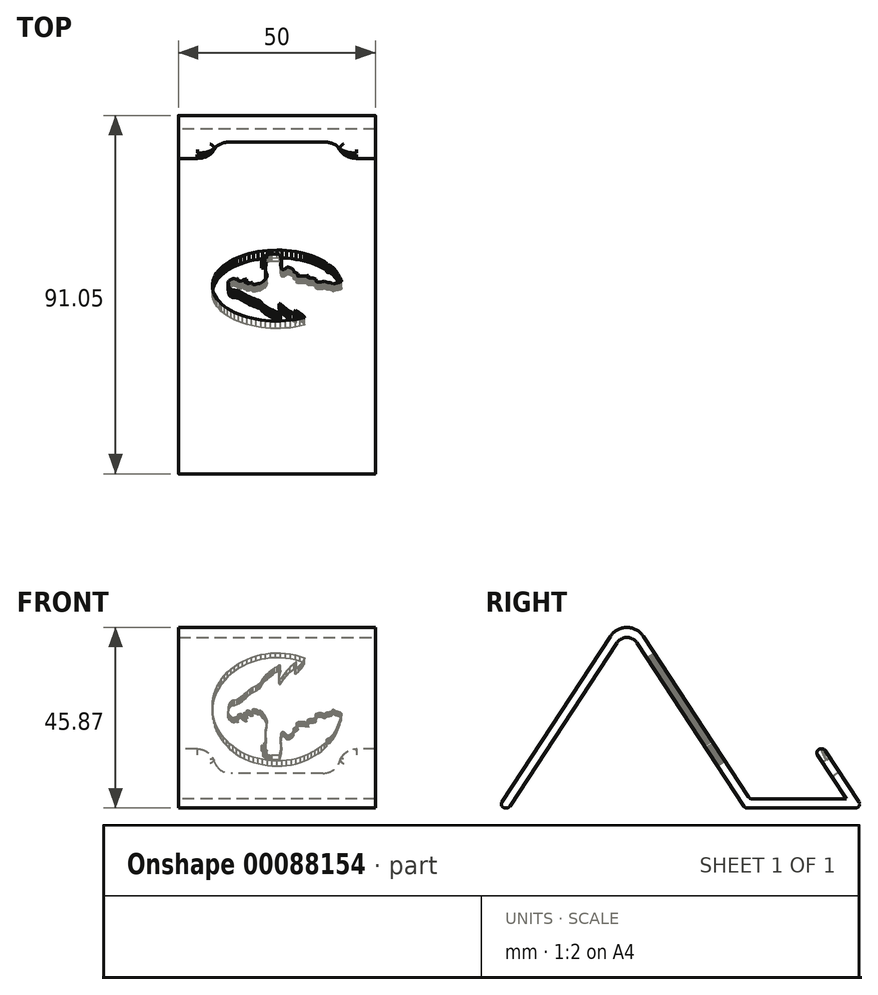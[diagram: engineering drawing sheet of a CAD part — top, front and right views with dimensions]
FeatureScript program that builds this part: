
annotation { "Feature Type Name" : "Feature", "Feature Type Description" : "" }
export const myFeature = defineFeature(function(context is Context, id is Id, definition is map)
    precondition{}
    {
        {
            var Q0;
            Q0=qCreatedBy(makeId("Right.planeOp"),FACE);
            var sketch = newSketch(context, id + "F0", { "sketchPlane" : qUnion([Q0])});
            skLineSegment(sketch, "E0", {"start": v(0, 0) * mm, "end": v(30, 45.8) * mm});
            skLineSegment(sketch, "E1", {"start": v(30, 45.8) * mm, "end": v(60, 0) * mm});
            skLineSegment(sketch, "E2", {"start": v(60, 0) * mm, "end": v(90, 0) * mm});
            skLineSegment(sketch, "E3", {"start": v(90, 0) * mm, "end": v(80.18, 15) * mm});
            skLineSegment(sketch, "E4.0", {"start": v(85.74, 2.3) * mm, "end": v(77.43, 15) * mm});
            skLineSegment(sketch, "E4.1", {"start": v(61.24, 2.3) * mm, "end": v(85.74, 2.3) * mm});
            skLineSegment(sketch, "E4.2", {"start": v(30, 50) * mm, "end": v(61.24, 2.3) * mm});
            skLineSegment(sketch, "E4.3", {"start": v(-2.75, 0) * mm, "end": v(30, 50) * mm});
            skLineSegment(sketch, "E5", {"start": v(80.18, 15) * mm, "end": v(77.43, 15) * mm});
            skLineSegment(sketch, "E6", {"start": v(-2.75, 0) * mm, "end": v(0, 0) * mm});
            skSolve(sketch);
        }
        {
            var Q0;
            Q0 = qSketchRegion(id + "F0", true);
            extrude(context, id + "F1", {"entities" : qUnion([Q0]), "depth" : 50 * mm});
        }
        {
            var Q0;
            Q0=makeQuery(id+"F1.opExtrude","SWEPT_FACE",FACE,{"disambiguationData":[OSD([sQuery(id+"F0.wireOp",EDGE,"E3")])]});
            var sketch = newSketch(context, id + "F2", { "sketchPlane" : qUnion([Q0])});
            skLineSegment(sketch, "E7", {"start": v(-43.27, -27.96) * mm, "end": v(-39.5, -38.31) * mm});
            skLineSegment(sketch, "E8", {"start": v(-39.5, -38.31) * mm, "end": v(-10.5, -38.31) * mm});
            skLineSegment(sketch, "E9", {"start": v(-10.5, -38.31) * mm, "end": v(-6.73, -27.96) * mm});
            skLineSegment(sketch, "E10", {"start": v(-6.73, -27.96) * mm, "end": v(-43.27, -27.96) * mm});
            skLineSegment(sketch, "E11", {"start": v(-25, -49.31) * mm, "end": v(-25, -35.25) * mm, "construction": true});
            skSolve(sketch);
        }
        {
            var Q0;
            {var subQ0=sQuery(id+"F2.wireOp",EDGE,"E8");Q0=makeQuery(id+"F2.imprint","IMPRINT",FACE,{"disambiguationData":[TD([[makeQuery(id+"F2.imprint","IMPRINT",EDGE,{"derivedFrom":subQ0}),1.0]])]});}
            var Q1;
            {var subQ0=sQuery(id+"F2.wireOp",EDGE,"E10");Q1=makeQuery(id+"F2.imprint","IMPRINT",FACE,{"disambiguationData":[TD([[makeQuery(id+"F2.imprint","IMPRINT",EDGE,{"derivedFrom":subQ0}),1.0]])]});}
            var Q2;
            Q2=makeQuery(id+"F1.opExtrude","SWEPT_FACE",FACE,{"disambiguationData":[OSD([sQuery(id+"F0.wireOp",EDGE,"E4.0")])]});
            extrude(context, id + "F3", {"entities" : qUnion([Q0, Q1]), "operationType" : NewBodyOperationType.REMOVE, "endBound" : BoundingType.UP_TO_SURFACE, "oppositeDirection" : true, "endBoundEntityFace" : qUnion([Q2]), "depth" : 25 * mm});
        }
        {
            var Q0;
            Q0=makeQuery(id+"F3.boolean.opBoolean","INTERSECT",EDGE,{"derivedFrom":[makeQuery(id+"F1.opExtrude","SWEPT_FACE",FACE,{"disambiguationData":[OSD([sQuery(id+"F0.wireOp",EDGE,"E5")])]}),makeQuery(id+"F3.opExtrude","SWEPT_FACE",FACE,{"disambiguationData":[OSD([sQuery(id+"F2.wireOp",EDGE,"E7")])]})]});
            var Q1;
            Q1=makeQuery(id+"F3.boolean.opBoolean","INTERSECT",EDGE,{"derivedFrom":[makeQuery(id+"F1.opExtrude","SWEPT_FACE",FACE,{"disambiguationData":[OSD([sQuery(id+"F0.wireOp",EDGE,"E5")])]}),makeQuery(id+"F3.opExtrude","SWEPT_FACE",FACE,{"disambiguationData":[OSD([sQuery(id+"F2.wireOp",EDGE,"E9")])]})]});
            var Q2;
            Q2=makeQuery(id+"F3.boolean.opBoolean","COPY",EDGE,{"derivedFrom":makeQuery(id+"F3.opExtrude","SWEPT_EDGE",EDGE,{"disambiguationData":[OSD([sQuery(id+"F2.wireOp",EDGE,"E7"),sQuery(id+"F2.wireOp",EDGE,"E8")])]})});
            var Q3;
            Q3=makeQuery(id+"F3.boolean.opBoolean","COPY",EDGE,{"derivedFrom":makeQuery(id+"F3.opExtrude","SWEPT_EDGE",EDGE,{"disambiguationData":[OSD([sQuery(id+"F2.wireOp",EDGE,"E8"),sQuery(id+"F2.wireOp",EDGE,"E9")])]})});
            fillet(context, id + "F4", {"entities" : qUnion([Q0, Q1, Q2, Q3]), "radius" : 4 * mm, "tangentPropagation" : true, "allowEdgeOverflow" : false});
        }
        {
            var Q0;
            Q0=makeQuery(id+"F1.opExtrude","SWEPT_EDGE",EDGE,{"disambiguationData":[OSD([sQuery(id+"F0.wireOp",EDGE,"E4.1"),sQuery(id+"F0.wireOp",EDGE,"E4.2")])]});
            var Q1;
            Q1=makeQuery(id+"F1.opExtrude","SWEPT_EDGE",EDGE,{"disambiguationData":[OSD([sQuery(id+"F0.wireOp",EDGE,"E4.0"),sQuery(id+"F0.wireOp",EDGE,"E5")])]});
            var Q2;
            Q2=makeQuery(id+"F1.opExtrude","SWEPT_EDGE",EDGE,{"disambiguationData":[OSD([sQuery(id+"F0.wireOp",EDGE,"E3"),sQuery(id+"F0.wireOp",EDGE,"E5")])]});
            var Q3;
            Q3=makeQuery(id+"F1.opExtrude","SWEPT_EDGE",EDGE,{"disambiguationData":[OSD([sQuery(id+"F0.wireOp",EDGE,"E2"),sQuery(id+"F0.wireOp",EDGE,"E3")])]});
            var Q4;
            Q4=makeQuery(id+"F1.opExtrude","SWEPT_EDGE",EDGE,{"disambiguationData":[OSD([sQuery(id+"F0.wireOp",EDGE,"E1"),sQuery(id+"F0.wireOp",EDGE,"E2")])]});
            var Q5;
            Q5=makeQuery(id+"F1.opExtrude","SWEPT_EDGE",EDGE,{"disambiguationData":[OSD([sQuery(id+"F0.wireOp",EDGE,"E0"),sQuery(id+"F0.wireOp",EDGE,"E6")])]});
            var Q6;
            Q6=makeQuery(id+"F1.opExtrude","SWEPT_EDGE",EDGE,{"disambiguationData":[OSD([sQuery(id+"F0.wireOp",EDGE,"E4.3"),sQuery(id+"F0.wireOp",EDGE,"E6")])]});
            var Q7;
            Q7=makeQuery(id+"F3.boolean.opBoolean","COPY",EDGE,{"derivedFrom":makeQuery(id+"F3.opExtrude","CAP_EDGE",EDGE,{"disambiguationData":[OSD([sQuery(id+"F2.wireOp",EDGE,"E8")])],"isStart":true})});
            var Q8;
            Q8=makeQuery(id+"F3.boolean.opBoolean","COPY",EDGE,{"derivedFrom":makeQuery(id+"F3.opExtrude","TWEAK_EDGE",EDGE,{"derivedFrom":[makeQuery(id+"F1.opExtrude","SWEPT_FACE",FACE,{"disambiguationData":[OSD([sQuery(id+"F0.wireOp",EDGE,"E4.0")])]}),makeQuery(id+"F2.imprint","IMPRINT",EDGE,{"derivedFrom":sQuery(id+"F2.wireOp",EDGE,"E8")})]})});
            fillet(context, id + "F5", {"entities" : qUnion([Q0, Q1, Q2, Q3, Q4, Q5, Q6, Q7, Q8]), "radius" : 1 * mm, "tangentPropagation" : true, "allowEdgeOverflow" : false});
        }
        {
            var Q0;
            Q0=makeQuery(id+"F1.opExtrude","SWEPT_EDGE",EDGE,{"disambiguationData":[OSD([sQuery(id+"F0.wireOp",EDGE,"E4.2"),sQuery(id+"F0.wireOp",EDGE,"E4.3")])]});
            fillet(context, id + "F6", {"entities" : qUnion([Q0]), "radius" : 5 * mm, "tangentPropagation" : true, "allowEdgeOverflow" : false});
        }
        {
            var Q0;
            Q0=makeQuery(id+"F1.opExtrude","SWEPT_EDGE",EDGE,{"disambiguationData":[OSD([sQuery(id+"F0.wireOp",EDGE,"E0"),sQuery(id+"F0.wireOp",EDGE,"E1")])]});
            fillet(context, id + "F7", {"entities" : qUnion([Q0]), "radius" : 3 * mm, "tangentPropagation" : true, "allowEdgeOverflow" : false});
        }
        {
            var Q0;
            Q0=makeQuery(id+"F1.opExtrude","SWEPT_FACE",FACE,{"disambiguationData":[OSD([sQuery(id+"F0.wireOp",EDGE,"E4.2")])]});
            var sketch = newSketch(context, id + "F8", { "sketchPlane" : qUnion([Q0])});
            skLineSegment(sketch, "E12", {"start": v(-35.93, 10.12) * mm, "end": v(-35.3, 10.38) * mm});
            skLineSegment(sketch, "E13", {"start": v(-35.3, 10.38) * mm, "end": v(-34.69, 10.72) * mm});
            skLineSegment(sketch, "E14", {"start": v(-34.69, 10.72) * mm, "end": v(-34.1, 11.12) * mm});
            skLineSegment(sketch, "E15", {"start": v(-34.1, 11.12) * mm, "end": v(-33.5, 11.53) * mm});
            skLineSegment(sketch, "E16", {"start": v(-33.5, 11.53) * mm, "end": v(-32.9, 11.93) * mm});
            skLineSegment(sketch, "E17", {"start": v(-32.9, 11.93) * mm, "end": v(-32.26, 12.27) * mm});
            skLineSegment(sketch, "E18", {"start": v(-32.26, 12.27) * mm, "end": v(-31.58, 12.52) * mm});
            skLineSegment(sketch, "E19", {"start": v(-31.58, 12.52) * mm, "end": v(-30.85, 12.63) * mm});
            skLineSegment(sketch, "E20", {"start": v(-30.85, 12.63) * mm, "end": v(-29.58, 13.07) * mm});
            skLineSegment(sketch, "E21", {"start": v(-29.58, 13.07) * mm, "end": v(-28.28, 13.38) * mm});
            skLineSegment(sketch, "E22", {"start": v(-28.28, 13.38) * mm, "end": v(-26.95, 13.54) * mm});
            skLineSegment(sketch, "E23", {"start": v(-26.95, 13.54) * mm, "end": v(-25.6, 13.52) * mm});
            skLineSegment(sketch, "E24", {"start": v(-25.6, 13.52) * mm, "end": v(-24.64, 13.55) * mm});
            skLineSegment(sketch, "E25", {"start": v(-24.64, 13.55) * mm, "end": v(-23.68, 13.5) * mm});
            skLineSegment(sketch, "E26", {"start": v(-23.68, 13.5) * mm, "end": v(-22.73, 13.4) * mm});
            skLineSegment(sketch, "E27", {"start": v(-22.73, 13.4) * mm, "end": v(-21.78, 13.24) * mm});
            skLineSegment(sketch, "E28", {"start": v(-21.78, 13.24) * mm, "end": v(-20.84, 13.04) * mm});
            skLineSegment(sketch, "E29", {"start": v(-20.84, 13.04) * mm, "end": v(-19.9, 12.82) * mm});
            skLineSegment(sketch, "E30", {"start": v(-19.9, 12.82) * mm, "end": v(-18.96, 12.58) * mm});
            skLineSegment(sketch, "E31", {"start": v(-18.96, 12.58) * mm, "end": v(-18.03, 12.35) * mm});
            skLineSegment(sketch, "E32", {"start": v(-18.03, 12.35) * mm, "end": v(-17.24, 11.84) * mm});
            skLineSegment(sketch, "E33", {"start": v(-17.24, 11.84) * mm, "end": v(-16.45, 11.33) * mm});
            skLineSegment(sketch, "E34", {"start": v(-16.45, 11.33) * mm, "end": v(-15.66, 10.82) * mm});
            skLineSegment(sketch, "E35", {"start": v(-15.66, 10.82) * mm, "end": v(-14.87, 10.3) * mm});
            skLineSegment(sketch, "E36", {"start": v(-14.87, 10.3) * mm, "end": v(-14.11, 9.74) * mm});
            skLineSegment(sketch, "E37", {"start": v(-14.11, 9.74) * mm, "end": v(-13.38, 9.16) * mm});
            skLineSegment(sketch, "E38", {"start": v(-13.38, 9.16) * mm, "end": v(-12.7, 8.52) * mm});
            skLineSegment(sketch, "E39", {"start": v(-12.7, 8.52) * mm, "end": v(-12.05, 7.83) * mm});
            skLineSegment(sketch, "E40", {"start": v(-12.05, 7.83) * mm, "end": v(-11.63, 7.46) * mm});
            skLineSegment(sketch, "E41", {"start": v(-11.63, 7.46) * mm, "end": v(-11.26, 7.07) * mm});
            skLineSegment(sketch, "E42", {"start": v(-11.26, 7.07) * mm, "end": v(-10.93, 6.64) * mm});
            skLineSegment(sketch, "E43", {"start": v(-10.93, 6.64) * mm, "end": v(-10.64, 6.2) * mm});
            skLineSegment(sketch, "E44", {"start": v(-10.64, 6.2) * mm, "end": v(-10.37, 5.72) * mm});
            skLineSegment(sketch, "E45", {"start": v(-10.37, 5.72) * mm, "end": v(-10.14, 5.23) * mm});
            skLineSegment(sketch, "E46", {"start": v(-10.14, 5.23) * mm, "end": v(-9.92, 4.74) * mm});
            skLineSegment(sketch, "E47", {"start": v(-9.92, 4.74) * mm, "end": v(-9.71, 4.23) * mm});
            skLineSegment(sketch, "E48", {"start": v(-9.71, 4.23) * mm, "end": v(-9.04, 2.68) * mm});
            skLineSegment(sketch, "E49", {"start": v(-9.04, 2.68) * mm, "end": v(-8.45, 1.1) * mm});
            skLineSegment(sketch, "E50", {"start": v(-8.45, 1.1) * mm, "end": v(-7.95, -0.52) * mm});
            skLineSegment(sketch, "E51", {"start": v(-7.95, -0.52) * mm, "end": v(-7.54, -2.16) * mm});
            skLineSegment(sketch, "E52", {"start": v(-7.54, -2.16) * mm, "end": v(-7.62, -3.8) * mm});
            skLineSegment(sketch, "E53", {"start": v(-7.62, -3.8) * mm, "end": v(-7.78, -5.45) * mm});
            skLineSegment(sketch, "E54", {"start": v(-7.78, -5.45) * mm, "end": v(-8.04, -7.08) * mm});
            skLineSegment(sketch, "E55", {"start": v(-8.04, -7.08) * mm, "end": v(-8.46, -8.68) * mm});
            skLineSegment(sketch, "E56", {"start": v(-8.46, -8.68) * mm, "end": v(-8.55, -9.28) * mm});
            skLineSegment(sketch, "E57", {"start": v(-8.55, -9.28) * mm, "end": v(-8.7, -9.85) * mm});
            skLineSegment(sketch, "E58", {"start": v(-8.7, -9.85) * mm, "end": v(-8.91, -10.4) * mm});
            skLineSegment(sketch, "E59", {"start": v(-8.91, -10.4) * mm, "end": v(-9.16, -10.94) * mm});
            skLineSegment(sketch, "E60", {"start": v(-9.16, -10.94) * mm, "end": v(-9.45, -11.46) * mm});
            skLineSegment(sketch, "E61", {"start": v(-9.45, -11.46) * mm, "end": v(-9.76, -11.97) * mm});
            skLineSegment(sketch, "E62", {"start": v(-9.76, -11.97) * mm, "end": v(-10.1, -12.46) * mm});
            skLineSegment(sketch, "E63", {"start": v(-10.1, -12.46) * mm, "end": v(-10.46, -12.94) * mm});
            skLineSegment(sketch, "E64", {"start": v(-10.46, -12.94) * mm, "end": v(-10.67, -13.27) * mm});
            skLineSegment(sketch, "E65", {"start": v(-10.67, -13.27) * mm, "end": v(-10.9, -13.6) * mm});
            skLineSegment(sketch, "E66", {"start": v(-10.9, -13.6) * mm, "end": v(-11.15, -13.93) * mm});
            skLineSegment(sketch, "E67", {"start": v(-11.15, -13.93) * mm, "end": v(-11.39, -14.26) * mm});
            skLineSegment(sketch, "E68", {"start": v(-11.39, -14.26) * mm, "end": v(-11.6, -14.59) * mm});
            skLineSegment(sketch, "E69", {"start": v(-11.6, -14.59) * mm, "end": v(-11.79, -14.92) * mm});
            skLineSegment(sketch, "E70", {"start": v(-11.79, -14.92) * mm, "end": v(-11.92, -15.25) * mm});
            skLineSegment(sketch, "E71", {"start": v(-11.92, -15.25) * mm, "end": v(-12, -15.6) * mm});
            skLineSegment(sketch, "E72", {"start": v(-12, -15.6) * mm, "end": v(-12.45, -15.72) * mm});
            skLineSegment(sketch, "E73", {"start": v(-12.45, -15.72) * mm, "end": v(-12.88, -16) * mm});
            skLineSegment(sketch, "E74", {"start": v(-12.88, -16) * mm, "end": v(-13.3, -16.37) * mm});
            skLineSegment(sketch, "E75", {"start": v(-13.3, -16.37) * mm, "end": v(-13.7, -16.81) * mm});
            skLineSegment(sketch, "E76", {"start": v(-13.7, -16.81) * mm, "end": v(-14.12, -17.26) * mm});
            skLineSegment(sketch, "E77", {"start": v(-14.12, -17.26) * mm, "end": v(-14.57, -17.68) * mm});
            skLineSegment(sketch, "E78", {"start": v(-14.57, -17.68) * mm, "end": v(-15.04, -18.03) * mm});
            skLineSegment(sketch, "E79", {"start": v(-15.04, -18.03) * mm, "end": v(-15.56, -18.26) * mm});
            skLineSegment(sketch, "E80", {"start": v(-15.56, -18.26) * mm, "end": v(-16.48, -18.75) * mm});
            skLineSegment(sketch, "E81", {"start": v(-16.48, -18.75) * mm, "end": v(-17.4, -19.2) * mm});
            skLineSegment(sketch, "E82", {"start": v(-17.4, -19.2) * mm, "end": v(-18.35, -19.62) * mm});
            skLineSegment(sketch, "E83", {"start": v(-18.35, -19.62) * mm, "end": v(-19.32, -20) * mm});
            skLineSegment(sketch, "E84", {"start": v(-19.32, -20) * mm, "end": v(-20.3, -20.32) * mm});
            skLineSegment(sketch, "E85", {"start": v(-20.3, -20.32) * mm, "end": v(-21.3, -20.57) * mm});
            skLineSegment(sketch, "E86", {"start": v(-21.3, -20.57) * mm, "end": v(-22.31, -20.76) * mm});
            skLineSegment(sketch, "E87", {"start": v(-22.31, -20.76) * mm, "end": v(-23.35, -20.88) * mm});
            skLineSegment(sketch, "E88", {"start": v(-23.35, -20.88) * mm, "end": v(-23.73, -20.82) * mm});
            skLineSegment(sketch, "E89", {"start": v(-23.73, -20.82) * mm, "end": v(-24.09, -20.85) * mm});
            skLineSegment(sketch, "E90", {"start": v(-24.09, -20.85) * mm, "end": v(-24.43, -20.95) * mm});
            skLineSegment(sketch, "E91", {"start": v(-24.43, -20.95) * mm, "end": v(-24.74, -21.08) * mm});
            skLineSegment(sketch, "E92", {"start": v(-24.74, -21.08) * mm, "end": v(-25.05, -21.22) * mm});
            skLineSegment(sketch, "E93", {"start": v(-25.05, -21.22) * mm, "end": v(-25.34, -21.35) * mm});
            skLineSegment(sketch, "E94", {"start": v(-25.34, -21.35) * mm, "end": v(-25.63, -21.43) * mm});
            skLineSegment(sketch, "E95", {"start": v(-25.63, -21.43) * mm, "end": v(-25.91, -21.45) * mm});
            skLineSegment(sketch, "E96", {"start": v(-25.91, -21.45) * mm, "end": v(-26.1, -21.25) * mm});
            skLineSegment(sketch, "E97", {"start": v(-26.1, -21.25) * mm, "end": v(-26.34, -21.09) * mm});
            skLineSegment(sketch, "E98", {"start": v(-26.34, -21.09) * mm, "end": v(-26.59, -20.96) * mm});
            skLineSegment(sketch, "E99", {"start": v(-26.59, -20.96) * mm, "end": v(-26.86, -20.87) * mm});
            skLineSegment(sketch, "E100", {"start": v(-26.86, -20.87) * mm, "end": v(-27.15, -20.8) * mm});
            skLineSegment(sketch, "E101", {"start": v(-27.15, -20.8) * mm, "end": v(-27.45, -20.75) * mm});
            skLineSegment(sketch, "E102", {"start": v(-27.45, -20.75) * mm, "end": v(-27.77, -20.71) * mm});
            skLineSegment(sketch, "E103", {"start": v(-27.77, -20.71) * mm, "end": v(-28.1, -20.7) * mm});
            skLineSegment(sketch, "E104", {"start": v(-28.1, -20.7) * mm, "end": v(-28.42, -20.68) * mm});
            skLineSegment(sketch, "E105", {"start": v(-28.42, -20.68) * mm, "end": v(-28.76, -20.66) * mm});
            skLineSegment(sketch, "E106", {"start": v(-28.76, -20.66) * mm, "end": v(-29.09, -20.65) * mm});
            skLineSegment(sketch, "E107", {"start": v(-29.09, -20.65) * mm, "end": v(-29.42, -20.62) * mm});
            skLineSegment(sketch, "E108", {"start": v(-29.42, -20.62) * mm, "end": v(-29.74, -20.58) * mm});
            skLineSegment(sketch, "E109", {"start": v(-29.74, -20.58) * mm, "end": v(-30.05, -20.53) * mm});
            skLineSegment(sketch, "E110", {"start": v(-30.05, -20.53) * mm, "end": v(-30.34, -20.46) * mm});
            skLineSegment(sketch, "E111", {"start": v(-30.34, -20.46) * mm, "end": v(-30.62, -20.35) * mm});
            skLineSegment(sketch, "E112", {"start": v(-30.62, -20.35) * mm, "end": v(-33.64, -18.68) * mm});
            skLineSegment(sketch, "E113", {"start": v(-33.64, -18.68) * mm, "end": v(-36.67, -17.02) * mm});
            skLineSegment(sketch, "E114", {"start": v(-36.67, -17.02) * mm, "end": v(-36.86, -16.48) * mm});
            skLineSegment(sketch, "E115", {"start": v(-36.86, -16.48) * mm, "end": v(-37.15, -16) * mm});
            skLineSegment(sketch, "E116", {"start": v(-37.15, -16) * mm, "end": v(-37.5, -15.54) * mm});
            skLineSegment(sketch, "E117", {"start": v(-37.5, -15.54) * mm, "end": v(-37.91, -15.11) * mm});
            skLineSegment(sketch, "E118", {"start": v(-37.91, -15.11) * mm, "end": v(-38.34, -14.7) * mm});
            skLineSegment(sketch, "E119", {"start": v(-38.34, -14.7) * mm, "end": v(-38.78, -14.28) * mm});
            skLineSegment(sketch, "E120", {"start": v(-38.78, -14.28) * mm, "end": v(-39.2, -13.86) * mm});
            skLineSegment(sketch, "E121", {"start": v(-39.2, -13.86) * mm, "end": v(-39.57, -13.42) * mm});
            skLineSegment(sketch, "E122", {"start": v(-39.57, -13.42) * mm, "end": v(-39.92, -12.92) * mm});
            skLineSegment(sketch, "E123", {"start": v(-39.92, -12.92) * mm, "end": v(-40.2, -12.39) * mm});
            skLineSegment(sketch, "E124", {"start": v(-40.2, -12.39) * mm, "end": v(-40.45, -11.83) * mm});
            skLineSegment(sketch, "E125", {"start": v(-40.45, -11.83) * mm, "end": v(-40.67, -11.26) * mm});
            skLineSegment(sketch, "E126", {"start": v(-40.67, -11.26) * mm, "end": v(-40.86, -10.67) * mm});
            skLineSegment(sketch, "E127", {"start": v(-40.86, -10.67) * mm, "end": v(-41.05, -10.09) * mm});
            skLineSegment(sketch, "E128", {"start": v(-41.05, -10.09) * mm, "end": v(-41.24, -9.5) * mm});
            skLineSegment(sketch, "E129", {"start": v(-41.24, -9.5) * mm, "end": v(-41.45, -8.93) * mm});
            skLineSegment(sketch, "E130", {"start": v(-41.45, -8.93) * mm, "end": v(-41.84, -7.5) * mm});
            skLineSegment(sketch, "E131", {"start": v(-41.84, -7.5) * mm, "end": v(-42.15, -6.05) * mm});
            skLineSegment(sketch, "E132", {"start": v(-42.15, -6.05) * mm, "end": v(-42.37, -4.59) * mm});
            skLineSegment(sketch, "E133", {"start": v(-42.37, -4.59) * mm, "end": v(-42.53, -3.12) * mm});
            skLineSegment(sketch, "E134", {"start": v(-42.53, -3.12) * mm, "end": v(-42.42, -2.39) * mm});
            skLineSegment(sketch, "E135", {"start": v(-42.42, -2.39) * mm, "end": v(-42.32, -1.65) * mm});
            skLineSegment(sketch, "E136", {"start": v(-42.32, -1.65) * mm, "end": v(-42.22, -0.91) * mm});
            skLineSegment(sketch, "E137", {"start": v(-42.22, -0.91) * mm, "end": v(-42.1, -0.18) * mm});
            skLineSegment(sketch, "E138", {"start": v(-42.1, -0.18) * mm, "end": v(-41.96, 0.55) * mm});
            skLineSegment(sketch, "E139", {"start": v(-41.96, 0.55) * mm, "end": v(-41.76, 1.26) * mm});
            skLineSegment(sketch, "E140", {"start": v(-41.76, 1.26) * mm, "end": v(-41.5, 1.95) * mm});
            skLineSegment(sketch, "E141", {"start": v(-41.5, 1.95) * mm, "end": v(-41.16, 2.61) * mm});
            skLineSegment(sketch, "E142", {"start": v(-41.16, 2.61) * mm, "end": v(-40.92, 3.24) * mm});
            skLineSegment(sketch, "E143", {"start": v(-40.92, 3.24) * mm, "end": v(-40.66, 3.87) * mm});
            skLineSegment(sketch, "E144", {"start": v(-40.66, 3.87) * mm, "end": v(-40.4, 4.48) * mm});
            skLineSegment(sketch, "E145", {"start": v(-40.4, 4.48) * mm, "end": v(-40.1, 5.08) * mm});
            skLineSegment(sketch, "E146", {"start": v(-40.1, 5.08) * mm, "end": v(-39.75, 5.66) * mm});
            skLineSegment(sketch, "E147", {"start": v(-39.75, 5.66) * mm, "end": v(-39.37, 6.2) * mm});
            skLineSegment(sketch, "E148", {"start": v(-39.37, 6.2) * mm, "end": v(-38.93, 6.7) * mm});
            skLineSegment(sketch, "E149", {"start": v(-38.93, 6.7) * mm, "end": v(-38.43, 7.17) * mm});
            skLineSegment(sketch, "E150", {"start": v(-38.43, 7.17) * mm, "end": v(-38.07, 7.56) * mm});
            skLineSegment(sketch, "E151", {"start": v(-38.07, 7.56) * mm, "end": v(-37.7, 7.95) * mm});
            skLineSegment(sketch, "E152", {"start": v(-37.7, 7.95) * mm, "end": v(-37.31, 8.35) * mm});
            skLineSegment(sketch, "E153", {"start": v(-37.31, 8.35) * mm, "end": v(-36.95, 8.75) * mm});
            skLineSegment(sketch, "E154", {"start": v(-36.95, 8.75) * mm, "end": v(-36.65, 9.16) * mm});
            skLineSegment(sketch, "E155", {"start": v(-36.65, 9.16) * mm, "end": v(-36.42, 9.59) * mm});
            skLineSegment(sketch, "E156", {"start": v(-36.42, 9.59) * mm, "end": v(-36.29, 10.03) * mm});
            skLineSegment(sketch, "E157", {"start": v(-36.29, 10.03) * mm, "end": v(-36.27, 10.5) * mm});
            skLineSegment(sketch, "E158", {"start": v(-36.27, 10.5) * mm, "end": v(-36.13, 10.39) * mm});
            skLineSegment(sketch, "E159", {"start": v(-36.13, 10.39) * mm, "end": v(-35.93, 10.12) * mm});
            skLineSegment(sketch, "E160", {"start": v(-37.7, -14.03) * mm, "end": v(-37.05, -14.86) * mm});
            skLineSegment(sketch, "E161", {"start": v(-37.05, -14.86) * mm, "end": v(-36.34, -15.63) * mm});
            skLineSegment(sketch, "E162", {"start": v(-36.34, -15.63) * mm, "end": v(-35.56, -16.33) * mm});
            skLineSegment(sketch, "E163", {"start": v(-35.56, -16.33) * mm, "end": v(-34.72, -16.98) * mm});
            skLineSegment(sketch, "E164", {"start": v(-34.72, -16.98) * mm, "end": v(-33.85, -17.57) * mm});
            skLineSegment(sketch, "E165", {"start": v(-33.85, -17.57) * mm, "end": v(-32.93, -18.1) * mm});
            skLineSegment(sketch, "E166", {"start": v(-32.93, -18.1) * mm, "end": v(-32, -18.59) * mm});
            skLineSegment(sketch, "E167", {"start": v(-32, -18.59) * mm, "end": v(-31.04, -19.01) * mm});
            skLineSegment(sketch, "E168", {"start": v(-31.04, -19.01) * mm, "end": v(-29.87, -19.42) * mm});
            skLineSegment(sketch, "E169", {"start": v(-29.87, -19.42) * mm, "end": v(-28.68, -19.74) * mm});
            skLineSegment(sketch, "E170", {"start": v(-28.68, -19.74) * mm, "end": v(-27.47, -19.96) * mm});
            skLineSegment(sketch, "E171", {"start": v(-27.47, -19.96) * mm, "end": v(-26.25, -20.09) * mm});
            skLineSegment(sketch, "E172", {"start": v(-26.25, -20.09) * mm, "end": v(-25.02, -20.13) * mm});
            skLineSegment(sketch, "E173", {"start": v(-25.02, -20.13) * mm, "end": v(-23.8, -20.07) * mm});
            skLineSegment(sketch, "E174", {"start": v(-23.8, -20.07) * mm, "end": v(-22.57, -19.93) * mm});
            skLineSegment(sketch, "E175", {"start": v(-22.57, -19.93) * mm, "end": v(-21.36, -19.7) * mm});
            skLineSegment(sketch, "E176", {"start": v(-21.36, -19.7) * mm, "end": v(-20.18, -19.4) * mm});
            skLineSegment(sketch, "E177", {"start": v(-20.18, -19.4) * mm, "end": v(-19.01, -19) * mm});
            skLineSegment(sketch, "E178", {"start": v(-19.01, -19) * mm, "end": v(-17.89, -18.51) * mm});
            skLineSegment(sketch, "E179", {"start": v(-17.89, -18.51) * mm, "end": v(-16.8, -17.95) * mm});
            skLineSegment(sketch, "E180", {"start": v(-16.8, -17.95) * mm, "end": v(-15.75, -17.3) * mm});
            skLineSegment(sketch, "E181", {"start": v(-15.75, -17.3) * mm, "end": v(-14.76, -16.57) * mm});
            skLineSegment(sketch, "E182", {"start": v(-14.76, -16.57) * mm, "end": v(-13.83, -15.76) * mm});
            skLineSegment(sketch, "E183", {"start": v(-13.83, -15.76) * mm, "end": v(-12.97, -14.88) * mm});
            skLineSegment(sketch, "E184", {"start": v(-12.97, -14.88) * mm, "end": v(-12.15, -13.93) * mm});
            skLineSegment(sketch, "E185", {"start": v(-12.15, -13.93) * mm, "end": v(-11.42, -12.92) * mm});
            skLineSegment(sketch, "E186", {"start": v(-11.42, -12.92) * mm, "end": v(-10.76, -11.86) * mm});
            skLineSegment(sketch, "E187", {"start": v(-10.76, -11.86) * mm, "end": v(-10.2, -10.75) * mm});
            skLineSegment(sketch, "E188", {"start": v(-10.2, -10.75) * mm, "end": v(-9.72, -9.6) * mm});
            skLineSegment(sketch, "E189", {"start": v(-9.72, -9.6) * mm, "end": v(-9.32, -8.42) * mm});
            skLineSegment(sketch, "E190", {"start": v(-9.32, -8.42) * mm, "end": v(-9.02, -7.21) * mm});
            skLineSegment(sketch, "E191", {"start": v(-9.02, -7.21) * mm, "end": v(-8.8, -5.98) * mm});
            skLineSegment(sketch, "E192", {"start": v(-8.8, -5.98) * mm, "end": v(-8.67, -4.74) * mm});
            skLineSegment(sketch, "E193", {"start": v(-8.67, -4.74) * mm, "end": v(-8.63, -3.5) * mm});
            skLineSegment(sketch, "E194", {"start": v(-8.63, -3.5) * mm, "end": v(-8.69, -2.26) * mm});
            skLineSegment(sketch, "E195", {"start": v(-8.69, -2.26) * mm, "end": v(-8.84, -1.02) * mm});
            skLineSegment(sketch, "E196", {"start": v(-8.84, -1.02) * mm, "end": v(-9.08, 0.2) * mm});
            skLineSegment(sketch, "E197", {"start": v(-9.08, 0.2) * mm, "end": v(-9.42, 1.4) * mm});
            skLineSegment(sketch, "E198", {"start": v(-9.42, 1.4) * mm, "end": v(-9.85, 2.57) * mm});
            skLineSegment(sketch, "E199", {"start": v(-9.85, 2.57) * mm, "end": v(-10.38, 3.7) * mm});
            skLineSegment(sketch, "E200", {"start": v(-10.38, 3.7) * mm, "end": v(-11, 4.82) * mm});
            skLineSegment(sketch, "E201", {"start": v(-11, 4.82) * mm, "end": v(-11.7, 5.88) * mm});
            skLineSegment(sketch, "E202", {"start": v(-11.7, 5.88) * mm, "end": v(-12.48, 6.87) * mm});
            skLineSegment(sketch, "E203", {"start": v(-12.48, 6.87) * mm, "end": v(-13.34, 7.8) * mm});
            skLineSegment(sketch, "E204", {"start": v(-13.34, 7.8) * mm, "end": v(-14.27, 8.66) * mm});
            skLineSegment(sketch, "E205", {"start": v(-14.27, 8.66) * mm, "end": v(-15.26, 9.45) * mm});
            skLineSegment(sketch, "E206", {"start": v(-15.26, 9.45) * mm, "end": v(-16.3, 10.16) * mm});
            skLineSegment(sketch, "E207", {"start": v(-16.3, 10.16) * mm, "end": v(-17.4, 10.8) * mm});
            skLineSegment(sketch, "E208", {"start": v(-17.4, 10.8) * mm, "end": v(-18.54, 11.34) * mm});
            skLineSegment(sketch, "E209", {"start": v(-18.54, 11.34) * mm, "end": v(-19.72, 11.8) * mm});
            skLineSegment(sketch, "E210", {"start": v(-19.72, 11.8) * mm, "end": v(-20.93, 12.17) * mm});
            skLineSegment(sketch, "E211", {"start": v(-20.93, 12.17) * mm, "end": v(-22.17, 12.45) * mm});
            skLineSegment(sketch, "E212", {"start": v(-22.17, 12.45) * mm, "end": v(-23.42, 12.63) * mm});
            skLineSegment(sketch, "E213", {"start": v(-23.42, 12.63) * mm, "end": v(-24.68, 12.7) * mm});
            skLineSegment(sketch, "E214", {"start": v(-24.68, 12.7) * mm, "end": v(-25.95, 12.68) * mm});
            skLineSegment(sketch, "E215", {"start": v(-25.95, 12.68) * mm, "end": v(-27.22, 12.54) * mm});
            skLineSegment(sketch, "E216", {"start": v(-27.22, 12.54) * mm, "end": v(-28.45, 12.33) * mm});
            skLineSegment(sketch, "E217", {"start": v(-28.45, 12.33) * mm, "end": v(-29.66, 12.03) * mm});
            skLineSegment(sketch, "E218", {"start": v(-29.66, 12.03) * mm, "end": v(-30.85, 11.63) * mm});
            skLineSegment(sketch, "E219", {"start": v(-30.85, 11.63) * mm, "end": v(-32, 11.13) * mm});
            skLineSegment(sketch, "E220", {"start": v(-32, 11.13) * mm, "end": v(-31.96, 10.9) * mm});
            skLineSegment(sketch, "E221", {"start": v(-31.96, 10.9) * mm, "end": v(-31.9, 10.66) * mm});
            skLineSegment(sketch, "E222", {"start": v(-31.9, 10.66) * mm, "end": v(-31.8, 10.41) * mm});
            skLineSegment(sketch, "E223", {"start": v(-31.8, 10.41) * mm, "end": v(-31.66, 10.16) * mm});
            skLineSegment(sketch, "E224", {"start": v(-31.66, 10.16) * mm, "end": v(-31.52, 9.9) * mm});
            skLineSegment(sketch, "E225", {"start": v(-31.52, 9.9) * mm, "end": v(-31.35, 9.65) * mm});
            skLineSegment(sketch, "E226", {"start": v(-31.35, 9.65) * mm, "end": v(-31.17, 9.4) * mm});
            skLineSegment(sketch, "E227", {"start": v(-31.17, 9.4) * mm, "end": v(-30.99, 9.16) * mm});
            skLineSegment(sketch, "E228", {"start": v(-30.99, 9.16) * mm, "end": v(-30.8, 8.93) * mm});
            skLineSegment(sketch, "E229", {"start": v(-30.8, 8.93) * mm, "end": v(-30.61, 8.7) * mm});
            skLineSegment(sketch, "E230", {"start": v(-30.61, 8.7) * mm, "end": v(-30.43, 8.5) * mm});
            skLineSegment(sketch, "E231", {"start": v(-30.43, 8.5) * mm, "end": v(-30.25, 8.3) * mm});
            skLineSegment(sketch, "E232", {"start": v(-30.25, 8.3) * mm, "end": v(-30.1, 8.12) * mm});
            skLineSegment(sketch, "E233", {"start": v(-30.1, 8.12) * mm, "end": v(-29.95, 7.96) * mm});
            skLineSegment(sketch, "E234", {"start": v(-29.95, 7.96) * mm, "end": v(-29.83, 7.83) * mm});
            skLineSegment(sketch, "E235", {"start": v(-29.83, 7.83) * mm, "end": v(-29.74, 7.73) * mm});
            skLineSegment(sketch, "E236", {"start": v(-29.74, 7.73) * mm, "end": v(-29.64, 7.88) * mm});
            skLineSegment(sketch, "E237", {"start": v(-29.64, 7.88) * mm, "end": v(-29.6, 8.06) * mm});
            skLineSegment(sketch, "E238", {"start": v(-29.6, 8.06) * mm, "end": v(-29.59, 8.28) * mm});
            skLineSegment(sketch, "E239", {"start": v(-29.59, 8.28) * mm, "end": v(-29.6, 8.51) * mm});
            skLineSegment(sketch, "E240", {"start": v(-29.6, 8.51) * mm, "end": v(-29.65, 8.76) * mm});
            skLineSegment(sketch, "E241", {"start": v(-29.65, 8.76) * mm, "end": v(-29.7, 9) * mm});
            skLineSegment(sketch, "E242", {"start": v(-29.7, 9) * mm, "end": v(-29.77, 9.24) * mm});
            skLineSegment(sketch, "E243", {"start": v(-29.77, 9.24) * mm, "end": v(-29.84, 9.45) * mm});
            skLineSegment(sketch, "E244", {"start": v(-29.84, 9.45) * mm, "end": v(-29.9, 9.64) * mm});
            skLineSegment(sketch, "E245", {"start": v(-29.9, 9.64) * mm, "end": v(-29.93, 9.8) * mm});
            skLineSegment(sketch, "E246", {"start": v(-29.93, 9.8) * mm, "end": v(-29.94, 9.9) * mm});
            skLineSegment(sketch, "E247", {"start": v(-29.94, 9.9) * mm, "end": v(-29.92, 9.95) * mm});
            skLineSegment(sketch, "E248", {"start": v(-29.92, 9.95) * mm, "end": v(-29.86, 9.94) * mm});
            skLineSegment(sketch, "E249", {"start": v(-29.86, 9.94) * mm, "end": v(-29.75, 9.85) * mm});
            skLineSegment(sketch, "E250", {"start": v(-29.75, 9.85) * mm, "end": v(-29.6, 9.68) * mm});
            skLineSegment(sketch, "E251", {"start": v(-29.6, 9.68) * mm, "end": v(-29.36, 9.4) * mm});
            skLineSegment(sketch, "E252", {"start": v(-29.36, 9.4) * mm, "end": v(-28.37, 8.37) * mm});
            skLineSegment(sketch, "E253", {"start": v(-28.37, 8.37) * mm, "end": v(-27.46, 7.26) * mm});
            skLineSegment(sketch, "E254", {"start": v(-27.46, 7.26) * mm, "end": v(-26.65, 6.09) * mm});
            skLineSegment(sketch, "E255", {"start": v(-26.65, 6.09) * mm, "end": v(-25.93, 4.85) * mm});
            skLineSegment(sketch, "E256", {"start": v(-25.93, 4.85) * mm, "end": v(-25.84, 4.68) * mm});
            skLineSegment(sketch, "E257", {"start": v(-25.84, 4.68) * mm, "end": v(-25.75, 4.61) * mm});
            skLineSegment(sketch, "E258", {"start": v(-25.75, 4.61) * mm, "end": v(-25.68, 4.64) * mm});
            skLineSegment(sketch, "E259", {"start": v(-25.68, 4.64) * mm, "end": v(-25.62, 4.74) * mm});
            skLineSegment(sketch, "E260", {"start": v(-25.62, 4.74) * mm, "end": v(-25.57, 4.9) * mm});
            skLineSegment(sketch, "E261", {"start": v(-25.57, 4.9) * mm, "end": v(-25.54, 5.13) * mm});
            skLineSegment(sketch, "E262", {"start": v(-25.54, 5.13) * mm, "end": v(-25.51, 5.38) * mm});
            skLineSegment(sketch, "E263", {"start": v(-25.51, 5.38) * mm, "end": v(-25.5, 5.65) * mm});
            skLineSegment(sketch, "E264", {"start": v(-25.5, 5.65) * mm, "end": v(-25.48, 5.94) * mm});
            skLineSegment(sketch, "E265", {"start": v(-25.48, 5.94) * mm, "end": v(-25.48, 6.21) * mm});
            skLineSegment(sketch, "E266", {"start": v(-25.48, 6.21) * mm, "end": v(-25.48, 6.47) * mm});
            skLineSegment(sketch, "E267", {"start": v(-25.48, 6.47) * mm, "end": v(-25.5, 6.7) * mm});
            skLineSegment(sketch, "E268", {"start": v(-25.5, 6.7) * mm, "end": v(-25.5, 6.87) * mm});
            skLineSegment(sketch, "E269", {"start": v(-25.5, 6.87) * mm, "end": v(-25.52, 6.98) * mm});
            skLineSegment(sketch, "E270", {"start": v(-25.52, 6.98) * mm, "end": v(-25.54, 7.01) * mm});
            skLineSegment(sketch, "E271", {"start": v(-25.54, 7.01) * mm, "end": v(-25.56, 6.96) * mm});
            skLineSegment(sketch, "E272", {"start": v(-25.56, 6.96) * mm, "end": v(-25.59, 7.15) * mm});
            skLineSegment(sketch, "E273", {"start": v(-25.59, 7.15) * mm, "end": v(-25.63, 7.35) * mm});
            skLineSegment(sketch, "E274", {"start": v(-25.63, 7.35) * mm, "end": v(-25.68, 7.57) * mm});
            skLineSegment(sketch, "E275", {"start": v(-25.68, 7.57) * mm, "end": v(-25.73, 7.8) * mm});
            skLineSegment(sketch, "E276", {"start": v(-25.73, 7.8) * mm, "end": v(-25.78, 8.02) * mm});
            skLineSegment(sketch, "E277", {"start": v(-25.78, 8.02) * mm, "end": v(-25.83, 8.24) * mm});
            skLineSegment(sketch, "E278", {"start": v(-25.83, 8.24) * mm, "end": v(-25.87, 8.45) * mm});
            skLineSegment(sketch, "E279", {"start": v(-25.87, 8.45) * mm, "end": v(-25.9, 8.63) * mm});
            skLineSegment(sketch, "E280", {"start": v(-25.9, 8.63) * mm, "end": v(-25.9, 8.78) * mm});
            skLineSegment(sketch, "E281", {"start": v(-25.9, 8.78) * mm, "end": v(-25.88, 8.9) * mm});
            skLineSegment(sketch, "E282", {"start": v(-25.88, 8.9) * mm, "end": v(-25.83, 8.98) * mm});
            skLineSegment(sketch, "E283", {"start": v(-25.83, 8.98) * mm, "end": v(-25.75, 9) * mm});
            skLineSegment(sketch, "E284", {"start": v(-25.75, 9) * mm, "end": v(-25.63, 8.98) * mm});
            skLineSegment(sketch, "E285", {"start": v(-25.63, 8.98) * mm, "end": v(-25.47, 8.9) * mm});
            skLineSegment(sketch, "E286", {"start": v(-25.47, 8.9) * mm, "end": v(-25.26, 8.73) * mm});
            skLineSegment(sketch, "E287", {"start": v(-25.26, 8.73) * mm, "end": v(-25, 8.5) * mm});
            skLineSegment(sketch, "E288", {"start": v(-25, 8.5) * mm, "end": v(-24.46, 8.13) * mm});
            skLineSegment(sketch, "E289", {"start": v(-24.46, 8.13) * mm, "end": v(-23.95, 7.72) * mm});
            skLineSegment(sketch, "E290", {"start": v(-23.95, 7.72) * mm, "end": v(-23.47, 7.29) * mm});
            skLineSegment(sketch, "E291", {"start": v(-23.47, 7.29) * mm, "end": v(-23, 6.83) * mm});
            skLineSegment(sketch, "E292", {"start": v(-23, 6.83) * mm, "end": v(-22.56, 6.35) * mm});
            skLineSegment(sketch, "E293", {"start": v(-22.56, 6.35) * mm, "end": v(-22.13, 5.85) * mm});
            skLineSegment(sketch, "E294", {"start": v(-22.13, 5.85) * mm, "end": v(-21.72, 5.35) * mm});
            skLineSegment(sketch, "E295", {"start": v(-21.72, 5.35) * mm, "end": v(-21.32, 4.84) * mm});
            skLineSegment(sketch, "E296", {"start": v(-21.32, 4.84) * mm, "end": v(-21.25, 4.5) * mm});
            skLineSegment(sketch, "E297", {"start": v(-21.25, 4.5) * mm, "end": v(-21.14, 4.2) * mm});
            skLineSegment(sketch, "E298", {"start": v(-21.14, 4.2) * mm, "end": v(-21, 3.94) * mm});
            skLineSegment(sketch, "E299", {"start": v(-21, 3.94) * mm, "end": v(-20.84, 3.69) * mm});
            skLineSegment(sketch, "E300", {"start": v(-20.84, 3.69) * mm, "end": v(-20.65, 3.47) * mm});
            skLineSegment(sketch, "E301", {"start": v(-20.65, 3.47) * mm, "end": v(-20.43, 3.26) * mm});
            skLineSegment(sketch, "E302", {"start": v(-20.43, 3.26) * mm, "end": v(-20.2, 3.07) * mm});
            skLineSegment(sketch, "E303", {"start": v(-20.2, 3.07) * mm, "end": v(-19.96, 2.9) * mm});
            skLineSegment(sketch, "E304", {"start": v(-19.96, 2.9) * mm, "end": v(-19.7, 2.72) * mm});
            skLineSegment(sketch, "E305", {"start": v(-19.7, 2.72) * mm, "end": v(-19.45, 2.56) * mm});
            skLineSegment(sketch, "E306", {"start": v(-19.45, 2.56) * mm, "end": v(-19.19, 2.4) * mm});
            skLineSegment(sketch, "E307", {"start": v(-19.19, 2.4) * mm, "end": v(-18.93, 2.23) * mm});
            skLineSegment(sketch, "E308", {"start": v(-18.93, 2.23) * mm, "end": v(-18.67, 2.05) * mm});
            skLineSegment(sketch, "E309", {"start": v(-18.67, 2.05) * mm, "end": v(-18.42, 1.87) * mm});
            skLineSegment(sketch, "E310", {"start": v(-18.42, 1.87) * mm, "end": v(-18.18, 1.67) * mm});
            skLineSegment(sketch, "E311", {"start": v(-18.18, 1.67) * mm, "end": v(-17.96, 1.46) * mm});
            skLineSegment(sketch, "E312", {"start": v(-17.96, 1.46) * mm, "end": v(-17.53, 1.04) * mm});
            skLineSegment(sketch, "E313", {"start": v(-17.53, 1.04) * mm, "end": v(-17.1, 0.58) * mm});
            skLineSegment(sketch, "E314", {"start": v(-17.1, 0.58) * mm, "end": v(-16.68, 0.1) * mm});
            skLineSegment(sketch, "E315", {"start": v(-16.68, 0.1) * mm, "end": v(-16.25, -0.36) * mm});
            skLineSegment(sketch, "E316", {"start": v(-16.25, -0.36) * mm, "end": v(-15.8, -0.8) * mm});
            skLineSegment(sketch, "E317", {"start": v(-15.8, -0.8) * mm, "end": v(-15.33, -1.18) * mm});
            skLineSegment(sketch, "E318", {"start": v(-15.33, -1.18) * mm, "end": v(-14.82, -1.5) * mm});
            skLineSegment(sketch, "E319", {"start": v(-14.82, -1.5) * mm, "end": v(-14.27, -1.71) * mm});
            skLineSegment(sketch, "E320", {"start": v(-14.27, -1.71) * mm, "end": v(-13.97, -1.68) * mm});
            skLineSegment(sketch, "E321", {"start": v(-13.97, -1.68) * mm, "end": v(-13.71, -1.72) * mm});
            skLineSegment(sketch, "E322", {"start": v(-13.71, -1.72) * mm, "end": v(-13.5, -1.81) * mm});
            skLineSegment(sketch, "E323", {"start": v(-13.5, -1.81) * mm, "end": v(-13.31, -1.96) * mm});
            skLineSegment(sketch, "E324", {"start": v(-13.31, -1.96) * mm, "end": v(-13.16, -2.15) * mm});
            skLineSegment(sketch, "E325", {"start": v(-13.16, -2.15) * mm, "end": v(-13.04, -2.39) * mm});
            skLineSegment(sketch, "E326", {"start": v(-13.04, -2.39) * mm, "end": v(-12.94, -2.65) * mm});
            skLineSegment(sketch, "E327", {"start": v(-12.94, -2.65) * mm, "end": v(-12.87, -2.94) * mm});
            skLineSegment(sketch, "E328", {"start": v(-12.87, -2.94) * mm, "end": v(-12.81, -3.24) * mm});
            skLineSegment(sketch, "E329", {"start": v(-12.81, -3.24) * mm, "end": v(-12.77, -3.56) * mm});
            skLineSegment(sketch, "E330", {"start": v(-12.77, -3.56) * mm, "end": v(-12.73, -3.88) * mm});
            skLineSegment(sketch, "E331", {"start": v(-12.73, -3.88) * mm, "end": v(-12.7, -4.2) * mm});
            skLineSegment(sketch, "E332", {"start": v(-12.7, -4.2) * mm, "end": v(-12.68, -4.5) * mm});
            skLineSegment(sketch, "E333", {"start": v(-12.68, -4.5) * mm, "end": v(-12.66, -4.79) * mm});
            skLineSegment(sketch, "E334", {"start": v(-12.66, -4.79) * mm, "end": v(-12.63, -5.05) * mm});
            skLineSegment(sketch, "E335", {"start": v(-12.63, -5.05) * mm, "end": v(-12.6, -5.29) * mm});
            skLineSegment(sketch, "E336", {"start": v(-12.6, -5.29) * mm, "end": v(-12.63, -5.5) * mm});
            skLineSegment(sketch, "E337", {"start": v(-12.63, -5.5) * mm, "end": v(-12.7, -5.72) * mm});
            skLineSegment(sketch, "E338", {"start": v(-12.7, -5.72) * mm, "end": v(-12.8, -5.93) * mm});
            skLineSegment(sketch, "E339", {"start": v(-12.8, -5.93) * mm, "end": v(-12.9, -6.12) * mm});
            skLineSegment(sketch, "E340", {"start": v(-12.9, -6.12) * mm, "end": v(-13.03, -6.31) * mm});
            skLineSegment(sketch, "E341", {"start": v(-13.03, -6.31) * mm, "end": v(-13.17, -6.48) * mm});
            skLineSegment(sketch, "E342", {"start": v(-13.17, -6.48) * mm, "end": v(-13.32, -6.63) * mm});
            skLineSegment(sketch, "E343", {"start": v(-13.32, -6.63) * mm, "end": v(-13.48, -6.76) * mm});
            skLineSegment(sketch, "E344", {"start": v(-13.48, -6.76) * mm, "end": v(-13.64, -6.86) * mm});
            skLineSegment(sketch, "E345", {"start": v(-13.64, -6.86) * mm, "end": v(-13.8, -6.93) * mm});
            skLineSegment(sketch, "E346", {"start": v(-13.8, -6.93) * mm, "end": v(-13.95, -6.97) * mm});
            skLineSegment(sketch, "E347", {"start": v(-13.95, -6.97) * mm, "end": v(-14.1, -6.97) * mm});
            skLineSegment(sketch, "E348", {"start": v(-14.1, -6.97) * mm, "end": v(-14.22, -6.94) * mm});
            skLineSegment(sketch, "E349", {"start": v(-14.22, -6.94) * mm, "end": v(-14.34, -6.85) * mm});
            skLineSegment(sketch, "E350", {"start": v(-14.34, -6.85) * mm, "end": v(-14.44, -6.72) * mm});
            skLineSegment(sketch, "E351", {"start": v(-14.44, -6.72) * mm, "end": v(-14.51, -6.54) * mm});
            skLineSegment(sketch, "E352", {"start": v(-14.51, -6.54) * mm, "end": v(-14.71, -6.76) * mm});
            skLineSegment(sketch, "E353", {"start": v(-14.71, -6.76) * mm, "end": v(-14.86, -6.9) * mm});
            skLineSegment(sketch, "E354", {"start": v(-14.86, -6.9) * mm, "end": v(-14.96, -6.98) * mm});
            skLineSegment(sketch, "E355", {"start": v(-14.96, -6.98) * mm, "end": v(-15.02, -6.99) * mm});
            skLineSegment(sketch, "E356", {"start": v(-15.02, -6.99) * mm, "end": v(-15.06, -6.94) * mm});
            skLineSegment(sketch, "E357", {"start": v(-15.06, -6.94) * mm, "end": v(-15.07, -6.86) * mm});
            skLineSegment(sketch, "E358", {"start": v(-15.07, -6.86) * mm, "end": v(-15.07, -6.74) * mm});
            skLineSegment(sketch, "E359", {"start": v(-15.07, -6.74) * mm, "end": v(-15.06, -6.6) * mm});
            skLineSegment(sketch, "E360", {"start": v(-15.06, -6.6) * mm, "end": v(-15.06, -6.44) * mm});
            skLineSegment(sketch, "E361", {"start": v(-15.06, -6.44) * mm, "end": v(-15.07, -6.28) * mm});
            skLineSegment(sketch, "E362", {"start": v(-15.07, -6.28) * mm, "end": v(-15.1, -6.12) * mm});
            skLineSegment(sketch, "E363", {"start": v(-15.1, -6.12) * mm, "end": v(-15.15, -5.98) * mm});
            skLineSegment(sketch, "E364", {"start": v(-15.15, -5.98) * mm, "end": v(-15.25, -5.86) * mm});
            skLineSegment(sketch, "E365", {"start": v(-15.25, -5.86) * mm, "end": v(-15.39, -5.77) * mm});
            skLineSegment(sketch, "E366", {"start": v(-15.39, -5.77) * mm, "end": v(-15.58, -5.73) * mm});
            skLineSegment(sketch, "E367", {"start": v(-15.58, -5.73) * mm, "end": v(-15.83, -5.73) * mm});
            skLineSegment(sketch, "E368", {"start": v(-15.83, -5.73) * mm, "end": v(-15.96, -5.88) * mm});
            skLineSegment(sketch, "E369", {"start": v(-15.96, -5.88) * mm, "end": v(-16.1, -6.03) * mm});
            skLineSegment(sketch, "E370", {"start": v(-16.1, -6.03) * mm, "end": v(-16.27, -6.17) * mm});
            skLineSegment(sketch, "E371", {"start": v(-16.27, -6.17) * mm, "end": v(-16.43, -6.3) * mm});
            skLineSegment(sketch, "E372", {"start": v(-16.43, -6.3) * mm, "end": v(-16.59, -6.42) * mm});
            skLineSegment(sketch, "E373", {"start": v(-16.59, -6.42) * mm, "end": v(-16.75, -6.52) * mm});
            skLineSegment(sketch, "E374", {"start": v(-16.75, -6.52) * mm, "end": v(-16.9, -6.6) * mm});
            skLineSegment(sketch, "E375", {"start": v(-16.9, -6.6) * mm, "end": v(-17.02, -6.67) * mm});
            skLineSegment(sketch, "E376", {"start": v(-17.02, -6.67) * mm, "end": v(-17.13, -6.7) * mm});
            skLineSegment(sketch, "E377", {"start": v(-17.13, -6.7) * mm, "end": v(-17.21, -6.7) * mm});
            skLineSegment(sketch, "E378", {"start": v(-17.21, -6.7) * mm, "end": v(-17.27, -6.67) * mm});
            skLineSegment(sketch, "E379", {"start": v(-17.27, -6.67) * mm, "end": v(-17.28, -6.6) * mm});
            skLineSegment(sketch, "E380", {"start": v(-17.28, -6.6) * mm, "end": v(-17.26, -6.48) * mm});
            skLineSegment(sketch, "E381", {"start": v(-17.26, -6.48) * mm, "end": v(-17.19, -6.33) * mm});
            skLineSegment(sketch, "E382", {"start": v(-17.19, -6.33) * mm, "end": v(-17.07, -6.12) * mm});
            skLineSegment(sketch, "E383", {"start": v(-17.07, -6.12) * mm, "end": v(-16.89, -5.86) * mm});
            skLineSegment(sketch, "E384", {"start": v(-16.89, -5.86) * mm, "end": v(-16.74, -5.63) * mm});
            skLineSegment(sketch, "E385", {"start": v(-16.74, -5.63) * mm, "end": v(-16.66, -5.49) * mm});
            skLineSegment(sketch, "E386", {"start": v(-16.66, -5.49) * mm, "end": v(-16.65, -5.4) * mm});
            skLineSegment(sketch, "E387", {"start": v(-16.65, -5.4) * mm, "end": v(-16.68, -5.38) * mm});
            skLineSegment(sketch, "E388", {"start": v(-16.68, -5.38) * mm, "end": v(-16.76, -5.39) * mm});
            skLineSegment(sketch, "E389", {"start": v(-16.76, -5.39) * mm, "end": v(-16.87, -5.43) * mm});
            skLineSegment(sketch, "E390", {"start": v(-16.87, -5.43) * mm, "end": v(-17, -5.5) * mm});
            skLineSegment(sketch, "E391", {"start": v(-17, -5.5) * mm, "end": v(-17.14, -5.56) * mm});
            skLineSegment(sketch, "E392", {"start": v(-17.14, -5.56) * mm, "end": v(-17.27, -5.63) * mm});
            skLineSegment(sketch, "E393", {"start": v(-17.27, -5.63) * mm, "end": v(-17.4, -5.68) * mm});
            skLineSegment(sketch, "E394", {"start": v(-17.4, -5.68) * mm, "end": v(-17.5, -5.71) * mm});
            skLineSegment(sketch, "E395", {"start": v(-17.5, -5.71) * mm, "end": v(-17.57, -5.7) * mm});
            skLineSegment(sketch, "E396", {"start": v(-17.57, -5.7) * mm, "end": v(-17.6, -5.66) * mm});
            skLineSegment(sketch, "E397", {"start": v(-17.6, -5.66) * mm, "end": v(-17.56, -5.54) * mm});
            skLineSegment(sketch, "E398", {"start": v(-17.56, -5.54) * mm, "end": v(-17.46, -5.37) * mm});
            skLineSegment(sketch, "E399", {"start": v(-17.46, -5.37) * mm, "end": v(-17.29, -5.1) * mm});
            skLineSegment(sketch, "E400", {"start": v(-17.29, -5.1) * mm, "end": v(-17.3, -4.87) * mm});
            skLineSegment(sketch, "E401", {"start": v(-17.3, -4.87) * mm, "end": v(-17.36, -4.73) * mm});
            skLineSegment(sketch, "E402", {"start": v(-17.36, -4.73) * mm, "end": v(-17.45, -4.65) * mm});
            skLineSegment(sketch, "E403", {"start": v(-17.45, -4.65) * mm, "end": v(-17.57, -4.64) * mm});
            skLineSegment(sketch, "E404", {"start": v(-17.57, -4.64) * mm, "end": v(-17.7, -4.67) * mm});
            skLineSegment(sketch, "E405", {"start": v(-17.7, -4.67) * mm, "end": v(-17.86, -4.73) * mm});
            skLineSegment(sketch, "E406", {"start": v(-17.86, -4.73) * mm, "end": v(-18.02, -4.82) * mm});
            skLineSegment(sketch, "E407", {"start": v(-18.02, -4.82) * mm, "end": v(-18.18, -4.92) * mm});
            skLineSegment(sketch, "E408", {"start": v(-18.18, -4.92) * mm, "end": v(-18.34, -5.01) * mm});
            skLineSegment(sketch, "E409", {"start": v(-18.34, -5.01) * mm, "end": v(-18.49, -5.09) * mm});
            skLineSegment(sketch, "E410", {"start": v(-18.49, -5.09) * mm, "end": v(-18.62, -5.13) * mm});
            skLineSegment(sketch, "E411", {"start": v(-18.62, -5.13) * mm, "end": v(-18.72, -5.14) * mm});
            skLineSegment(sketch, "E412", {"start": v(-18.72, -5.14) * mm, "end": v(-18.8, -5.09) * mm});
            skLineSegment(sketch, "E413", {"start": v(-18.8, -5.09) * mm, "end": v(-18.83, -4.97) * mm});
            skLineSegment(sketch, "E414", {"start": v(-18.83, -4.97) * mm, "end": v(-18.82, -4.77) * mm});
            skLineSegment(sketch, "E415", {"start": v(-18.82, -4.77) * mm, "end": v(-18.76, -4.47) * mm});
            skLineSegment(sketch, "E416", {"start": v(-18.76, -4.47) * mm, "end": v(-18.99, -4.24) * mm});
            skLineSegment(sketch, "E417", {"start": v(-18.99, -4.24) * mm, "end": v(-19.21, -4.18) * mm});
            skLineSegment(sketch, "E418", {"start": v(-19.21, -4.18) * mm, "end": v(-19.43, -4.24) * mm});
            skLineSegment(sketch, "E419", {"start": v(-19.43, -4.24) * mm, "end": v(-19.66, -4.37) * mm});
            skLineSegment(sketch, "E420", {"start": v(-19.66, -4.37) * mm, "end": v(-19.9, -4.52) * mm});
            skLineSegment(sketch, "E421", {"start": v(-19.9, -4.52) * mm, "end": v(-20.13, -4.64) * mm});
            skLineSegment(sketch, "E422", {"start": v(-20.13, -4.64) * mm, "end": v(-20.39, -4.68) * mm});
            skLineSegment(sketch, "E423", {"start": v(-20.39, -4.68) * mm, "end": v(-20.65, -4.6) * mm});
            skLineSegment(sketch, "E424", {"start": v(-20.65, -4.6) * mm, "end": v(-21.08, -5.1) * mm});
            skLineSegment(sketch, "E425", {"start": v(-21.08, -5.1) * mm, "end": v(-21.49, -5.63) * mm});
            skLineSegment(sketch, "E426", {"start": v(-21.49, -5.63) * mm, "end": v(-21.86, -6.2) * mm});
            skLineSegment(sketch, "E427", {"start": v(-21.86, -6.2) * mm, "end": v(-22.16, -6.78) * mm});
            skLineSegment(sketch, "E428", {"start": v(-22.16, -6.78) * mm, "end": v(-22.39, -7.38) * mm});
            skLineSegment(sketch, "E429", {"start": v(-22.39, -7.38) * mm, "end": v(-22.52, -7.99) * mm});
            skLineSegment(sketch, "E430", {"start": v(-22.52, -7.99) * mm, "end": v(-22.52, -8.6) * mm});
            skLineSegment(sketch, "E431", {"start": v(-22.52, -8.6) * mm, "end": v(-22.38, -9.2) * mm});
            skLineSegment(sketch, "E432", {"start": v(-22.38, -9.2) * mm, "end": v(-22.2, -9.88) * mm});
            skLineSegment(sketch, "E433", {"start": v(-22.2, -9.88) * mm, "end": v(-22.1, -10.57) * mm});
            skLineSegment(sketch, "E434", {"start": v(-22.1, -10.57) * mm, "end": v(-22.08, -11.26) * mm});
            skLineSegment(sketch, "E435", {"start": v(-22.08, -11.26) * mm, "end": v(-22.1, -11.94) * mm});
            skLineSegment(sketch, "E436", {"start": v(-22.1, -11.94) * mm, "end": v(-22.14, -12.63) * mm});
            skLineSegment(sketch, "E437", {"start": v(-22.14, -12.63) * mm, "end": v(-22.2, -13.33) * mm});
            skLineSegment(sketch, "E438", {"start": v(-22.2, -13.33) * mm, "end": v(-22.24, -14.03) * mm});
            skLineSegment(sketch, "E439", {"start": v(-22.24, -14.03) * mm, "end": v(-22.26, -14.74) * mm});
            skLineSegment(sketch, "E440", {"start": v(-22.26, -14.74) * mm, "end": v(-22, -14.67) * mm});
            skLineSegment(sketch, "E441", {"start": v(-22, -14.67) * mm, "end": v(-21.84, -14.65) * mm});
            skLineSegment(sketch, "E442", {"start": v(-21.84, -14.65) * mm, "end": v(-21.73, -14.67) * mm});
            skLineSegment(sketch, "E443", {"start": v(-21.73, -14.67) * mm, "end": v(-21.69, -14.72) * mm});
            skLineSegment(sketch, "E444", {"start": v(-21.69, -14.72) * mm, "end": v(-21.68, -14.8) * mm});
            skLineSegment(sketch, "E445", {"start": v(-21.68, -14.8) * mm, "end": v(-21.72, -14.9) * mm});
            skLineSegment(sketch, "E446", {"start": v(-21.72, -14.9) * mm, "end": v(-21.77, -15) * mm});
            skLineSegment(sketch, "E447", {"start": v(-21.77, -15) * mm, "end": v(-21.84, -15.13) * mm});
            skLineSegment(sketch, "E448", {"start": v(-21.84, -15.13) * mm, "end": v(-21.9, -15.25) * mm});
            skLineSegment(sketch, "E449", {"start": v(-21.9, -15.25) * mm, "end": v(-21.96, -15.36) * mm});
            skLineSegment(sketch, "E450", {"start": v(-21.96, -15.36) * mm, "end": v(-22, -15.45) * mm});
            skLineSegment(sketch, "E451", {"start": v(-22, -15.45) * mm, "end": v(-22, -15.53) * mm});
            skLineSegment(sketch, "E452", {"start": v(-22, -15.53) * mm, "end": v(-21.96, -15.57) * mm});
            skLineSegment(sketch, "E453", {"start": v(-21.96, -15.57) * mm, "end": v(-21.86, -15.58) * mm});
            skLineSegment(sketch, "E454", {"start": v(-21.86, -15.58) * mm, "end": v(-21.7, -15.55) * mm});
            skLineSegment(sketch, "E455", {"start": v(-21.7, -15.55) * mm, "end": v(-21.47, -15.47) * mm});
            skLineSegment(sketch, "E456", {"start": v(-21.47, -15.47) * mm, "end": v(-21.23, -15.41) * mm});
            skLineSegment(sketch, "E457", {"start": v(-21.23, -15.41) * mm, "end": v(-21.1, -15.42) * mm});
            skLineSegment(sketch, "E458", {"start": v(-21.1, -15.42) * mm, "end": v(-21.08, -15.48) * mm});
            skLineSegment(sketch, "E459", {"start": v(-21.08, -15.48) * mm, "end": v(-21.14, -15.58) * mm});
            skLineSegment(sketch, "E460", {"start": v(-21.14, -15.58) * mm, "end": v(-21.27, -15.72) * mm});
            skLineSegment(sketch, "E461", {"start": v(-21.27, -15.72) * mm, "end": v(-21.44, -15.89) * mm});
            skLineSegment(sketch, "E462", {"start": v(-21.44, -15.89) * mm, "end": v(-21.64, -16.07) * mm});
            skLineSegment(sketch, "E463", {"start": v(-21.64, -16.07) * mm, "end": v(-21.85, -16.26) * mm});
            skLineSegment(sketch, "E464", {"start": v(-21.85, -16.26) * mm, "end": v(-22.06, -16.46) * mm});
            skLineSegment(sketch, "E465", {"start": v(-22.06, -16.46) * mm, "end": v(-22.24, -16.64) * mm});
            skLineSegment(sketch, "E466", {"start": v(-22.24, -16.64) * mm, "end": v(-22.39, -16.8) * mm});
            skLineSegment(sketch, "E467", {"start": v(-22.39, -16.8) * mm, "end": v(-22.47, -16.95) * mm});
            skLineSegment(sketch, "E468", {"start": v(-22.47, -16.95) * mm, "end": v(-22.48, -17.05) * mm});
            skLineSegment(sketch, "E469", {"start": v(-22.48, -17.05) * mm, "end": v(-22.4, -17.1) * mm});
            skLineSegment(sketch, "E470", {"start": v(-22.4, -17.1) * mm, "end": v(-22.2, -17.11) * mm});
            skLineSegment(sketch, "E471", {"start": v(-22.2, -17.11) * mm, "end": v(-21.87, -17.06) * mm});
            skLineSegment(sketch, "E472", {"start": v(-21.87, -17.06) * mm, "end": v(-21.65, -17) * mm});
            skLineSegment(sketch, "E473", {"start": v(-21.65, -17) * mm, "end": v(-21.5, -17.01) * mm});
            skLineSegment(sketch, "E474", {"start": v(-21.5, -17.01) * mm, "end": v(-21.44, -17.06) * mm});
            skLineSegment(sketch, "E475", {"start": v(-21.44, -17.06) * mm, "end": v(-21.44, -17.14) * mm});
            skLineSegment(sketch, "E476", {"start": v(-21.44, -17.14) * mm, "end": v(-21.5, -17.25) * mm});
            skLineSegment(sketch, "E477", {"start": v(-21.5, -17.25) * mm, "end": v(-21.6, -17.38) * mm});
            skLineSegment(sketch, "E478", {"start": v(-21.6, -17.38) * mm, "end": v(-21.75, -17.53) * mm});
            skLineSegment(sketch, "E479", {"start": v(-21.75, -17.53) * mm, "end": v(-21.94, -17.68) * mm});
            skLineSegment(sketch, "E480", {"start": v(-21.94, -17.68) * mm, "end": v(-22.15, -17.84) * mm});
            skLineSegment(sketch, "E481", {"start": v(-22.15, -17.84) * mm, "end": v(-22.38, -17.99) * mm});
            skLineSegment(sketch, "E482", {"start": v(-22.38, -17.99) * mm, "end": v(-22.62, -18.12) * mm});
            skLineSegment(sketch, "E483", {"start": v(-22.62, -18.12) * mm, "end": v(-22.87, -18.23) * mm});
            skLineSegment(sketch, "E484", {"start": v(-22.87, -18.23) * mm, "end": v(-23.1, -18.3) * mm});
            skLineSegment(sketch, "E485", {"start": v(-23.1, -18.3) * mm, "end": v(-23.33, -18.35) * mm});
            skLineSegment(sketch, "E486", {"start": v(-23.33, -18.35) * mm, "end": v(-23.54, -18.35) * mm});
            skLineSegment(sketch, "E487", {"start": v(-23.54, -18.35) * mm, "end": v(-23.71, -18.3) * mm});
            skLineSegment(sketch, "E488", {"start": v(-23.71, -18.3) * mm, "end": v(-25.64, -18.3) * mm});
            skLineSegment(sketch, "E489", {"start": v(-25.64, -18.3) * mm, "end": v(-25.74, -17.68) * mm});
            skLineSegment(sketch, "E490", {"start": v(-25.74, -17.68) * mm, "end": v(-25.86, -17.07) * mm});
            skLineSegment(sketch, "E491", {"start": v(-25.86, -17.07) * mm, "end": v(-25.99, -16.48) * mm});
            skLineSegment(sketch, "E492", {"start": v(-25.99, -16.48) * mm, "end": v(-26.09, -15.89) * mm});
            skLineSegment(sketch, "E493", {"start": v(-26.09, -15.89) * mm, "end": v(-26.16, -15.3) * mm});
            skLineSegment(sketch, "E494", {"start": v(-26.16, -15.3) * mm, "end": v(-26.16, -14.7) * mm});
            skLineSegment(sketch, "E495", {"start": v(-26.16, -14.7) * mm, "end": v(-26.1, -14.08) * mm});
            skLineSegment(sketch, "E496", {"start": v(-26.1, -14.08) * mm, "end": v(-25.92, -13.45) * mm});
            skLineSegment(sketch, "E497", {"start": v(-25.92, -13.45) * mm, "end": v(-25.94, -13.27) * mm});
            skLineSegment(sketch, "E498", {"start": v(-25.94, -13.27) * mm, "end": v(-25.95, -13.05) * mm});
            skLineSegment(sketch, "E499", {"start": v(-25.95, -13.05) * mm, "end": v(-25.97, -12.81) * mm});
            skLineSegment(sketch, "E500", {"start": v(-25.97, -12.81) * mm, "end": v(-25.99, -12.56) * mm});
            skLineSegment(sketch, "E501", {"start": v(-25.99, -12.56) * mm, "end": v(-26.02, -12.3) * mm});
            skLineSegment(sketch, "E502", {"start": v(-26.02, -12.3) * mm, "end": v(-26.05, -12.04) * mm});
            skLineSegment(sketch, "E503", {"start": v(-26.05, -12.04) * mm, "end": v(-26.09, -11.8) * mm});
            skLineSegment(sketch, "E504", {"start": v(-26.09, -11.8) * mm, "end": v(-26.14, -11.58) * mm});
            skLineSegment(sketch, "E505", {"start": v(-26.14, -11.58) * mm, "end": v(-26.2, -11.39) * mm});
            skLineSegment(sketch, "E506", {"start": v(-26.2, -11.39) * mm, "end": v(-26.28, -11.24) * mm});
            skLineSegment(sketch, "E507", {"start": v(-26.28, -11.24) * mm, "end": v(-26.38, -11.14) * mm});
            skLineSegment(sketch, "E508", {"start": v(-26.38, -11.14) * mm, "end": v(-26.49, -11.1) * mm});
            skLineSegment(sketch, "E509", {"start": v(-26.49, -11.1) * mm, "end": v(-26.62, -11.11) * mm});
            skLineSegment(sketch, "E510", {"start": v(-26.62, -11.11) * mm, "end": v(-26.77, -11.2) * mm});
            skLineSegment(sketch, "E511", {"start": v(-26.77, -11.2) * mm, "end": v(-26.94, -11.4) * mm});
            skLineSegment(sketch, "E512", {"start": v(-26.94, -11.4) * mm, "end": v(-27.14, -11.67) * mm});
            skLineSegment(sketch, "E513", {"start": v(-27.14, -11.67) * mm, "end": v(-27.27, -11.92) * mm});
            skLineSegment(sketch, "E514", {"start": v(-27.27, -11.92) * mm, "end": v(-27.42, -12.1) * mm});
            skLineSegment(sketch, "E515", {"start": v(-27.42, -12.1) * mm, "end": v(-27.59, -12.21) * mm});
            skLineSegment(sketch, "E516", {"start": v(-27.59, -12.21) * mm, "end": v(-27.76, -12.25) * mm});
            skLineSegment(sketch, "E517", {"start": v(-27.76, -12.25) * mm, "end": v(-27.94, -12.24) * mm});
            skLineSegment(sketch, "E518", {"start": v(-27.94, -12.24) * mm, "end": v(-28.12, -12.18) * mm});
            skLineSegment(sketch, "E519", {"start": v(-28.12, -12.18) * mm, "end": v(-28.3, -12.07) * mm});
            skLineSegment(sketch, "E520", {"start": v(-28.3, -12.07) * mm, "end": v(-28.48, -11.94) * mm});
            skLineSegment(sketch, "E521", {"start": v(-28.48, -11.94) * mm, "end": v(-28.65, -11.77) * mm});
            skLineSegment(sketch, "E522", {"start": v(-28.65, -11.77) * mm, "end": v(-28.8, -11.59) * mm});
            skLineSegment(sketch, "E523", {"start": v(-28.8, -11.59) * mm, "end": v(-28.95, -11.4) * mm});
            skLineSegment(sketch, "E524", {"start": v(-28.95, -11.4) * mm, "end": v(-29.07, -11.2) * mm});
            skLineSegment(sketch, "E525", {"start": v(-29.07, -11.2) * mm, "end": v(-29.17, -11) * mm});
            skLineSegment(sketch, "E526", {"start": v(-29.17, -11) * mm, "end": v(-29.24, -10.8) * mm});
            skLineSegment(sketch, "E527", {"start": v(-29.24, -10.8) * mm, "end": v(-29.28, -10.64) * mm});
            skLineSegment(sketch, "E528", {"start": v(-29.28, -10.64) * mm, "end": v(-29.29, -10.5) * mm});
            skLineSegment(sketch, "E529", {"start": v(-29.29, -10.5) * mm, "end": v(-29.25, -10.35) * mm});
            skLineSegment(sketch, "E530", {"start": v(-29.25, -10.35) * mm, "end": v(-29.27, -10.2) * mm});
            skLineSegment(sketch, "E531", {"start": v(-29.27, -10.2) * mm, "end": v(-29.34, -10.08) * mm});
            skLineSegment(sketch, "E532", {"start": v(-29.34, -10.08) * mm, "end": v(-29.44, -9.97) * mm});
            skLineSegment(sketch, "E533", {"start": v(-29.44, -9.97) * mm, "end": v(-29.56, -9.86) * mm});
            skLineSegment(sketch, "E534", {"start": v(-29.56, -9.86) * mm, "end": v(-29.7, -9.76) * mm});
            skLineSegment(sketch, "E535", {"start": v(-29.7, -9.76) * mm, "end": v(-29.85, -9.66) * mm});
            skLineSegment(sketch, "E536", {"start": v(-29.85, -9.66) * mm, "end": v(-30, -9.56) * mm});
            skLineSegment(sketch, "E537", {"start": v(-30, -9.56) * mm, "end": v(-30.14, -9.46) * mm});
            skLineSegment(sketch, "E538", {"start": v(-30.14, -9.46) * mm, "end": v(-30.26, -9.35) * mm});
            skLineSegment(sketch, "E539", {"start": v(-30.26, -9.35) * mm, "end": v(-30.35, -9.24) * mm});
            skLineSegment(sketch, "E540", {"start": v(-30.35, -9.24) * mm, "end": v(-30.4, -9.11) * mm});
            skLineSegment(sketch, "E541", {"start": v(-30.4, -9.11) * mm, "end": v(-30.4, -8.98) * mm});
            skLineSegment(sketch, "E542", {"start": v(-30.4, -8.98) * mm, "end": v(-30.34, -8.83) * mm});
            skLineSegment(sketch, "E543", {"start": v(-30.34, -8.83) * mm, "end": v(-30.22, -8.67) * mm});
            skLineSegment(sketch, "E544", {"start": v(-30.22, -8.67) * mm, "end": v(-30.03, -8.49) * mm});
            skLineSegment(sketch, "E545", {"start": v(-30.03, -8.49) * mm, "end": v(-30.15, -8.34) * mm});
            skLineSegment(sketch, "E546", {"start": v(-30.15, -8.34) * mm, "end": v(-30.32, -8.24) * mm});
            skLineSegment(sketch, "E547", {"start": v(-30.32, -8.24) * mm, "end": v(-30.52, -8.16) * mm});
            skLineSegment(sketch, "E548", {"start": v(-30.52, -8.16) * mm, "end": v(-30.75, -8.12) * mm});
            skLineSegment(sketch, "E549", {"start": v(-30.75, -8.12) * mm, "end": v(-31, -8.1) * mm});
            skLineSegment(sketch, "E550", {"start": v(-31, -8.1) * mm, "end": v(-31.26, -8.09) * mm});
            skLineSegment(sketch, "E551", {"start": v(-31.26, -8.09) * mm, "end": v(-31.53, -8.1) * mm});
            skLineSegment(sketch, "E552", {"start": v(-31.53, -8.1) * mm, "end": v(-31.8, -8.13) * mm});
            skLineSegment(sketch, "E553", {"start": v(-31.8, -8.13) * mm, "end": v(-32.06, -8.16) * mm});
            skLineSegment(sketch, "E554", {"start": v(-32.06, -8.16) * mm, "end": v(-32.3, -8.2) * mm});
            skLineSegment(sketch, "E555", {"start": v(-32.3, -8.2) * mm, "end": v(-32.52, -8.24) * mm});
            skLineSegment(sketch, "E556", {"start": v(-32.52, -8.24) * mm, "end": v(-32.71, -8.28) * mm});
            skLineSegment(sketch, "E557", {"start": v(-32.71, -8.28) * mm, "end": v(-32.87, -8.3) * mm});
            skLineSegment(sketch, "E558", {"start": v(-32.87, -8.3) * mm, "end": v(-32.98, -8.33) * mm});
            skLineSegment(sketch, "E559", {"start": v(-32.98, -8.33) * mm, "end": v(-33.04, -8.34) * mm});
            skLineSegment(sketch, "E560", {"start": v(-33.04, -8.34) * mm, "end": v(-33.04, -8.33) * mm});
            skLineSegment(sketch, "E561", {"start": v(-33.04, -8.33) * mm, "end": v(-32.86, -8.01) * mm});
            skLineSegment(sketch, "E562", {"start": v(-32.86, -8.01) * mm, "end": v(-32.77, -7.77) * mm});
            skLineSegment(sketch, "E563", {"start": v(-32.77, -7.77) * mm, "end": v(-32.78, -7.58) * mm});
            skLineSegment(sketch, "E564", {"start": v(-32.78, -7.58) * mm, "end": v(-32.86, -7.45) * mm});
            skLineSegment(sketch, "E565", {"start": v(-32.86, -7.45) * mm, "end": v(-33, -7.36) * mm});
            skLineSegment(sketch, "E566", {"start": v(-33, -7.36) * mm, "end": v(-33.2, -7.3) * mm});
            skLineSegment(sketch, "E567", {"start": v(-33.2, -7.3) * mm, "end": v(-33.43, -7.26) * mm});
            skLineSegment(sketch, "E568", {"start": v(-33.43, -7.26) * mm, "end": v(-33.68, -7.22) * mm});
            skLineSegment(sketch, "E569", {"start": v(-33.68, -7.22) * mm, "end": v(-33.94, -7.19) * mm});
            skLineSegment(sketch, "E570", {"start": v(-33.94, -7.19) * mm, "end": v(-34.19, -7.15) * mm});
            skLineSegment(sketch, "E571", {"start": v(-34.19, -7.15) * mm, "end": v(-34.42, -7.08) * mm});
            skLineSegment(sketch, "E572", {"start": v(-34.42, -7.08) * mm, "end": v(-34.63, -6.98) * mm});
            skLineSegment(sketch, "E573", {"start": v(-34.63, -6.98) * mm, "end": v(-34.78, -6.84) * mm});
            skLineSegment(sketch, "E574", {"start": v(-34.78, -6.84) * mm, "end": v(-34.88, -6.65) * mm});
            skLineSegment(sketch, "E575", {"start": v(-34.88, -6.65) * mm, "end": v(-34.9, -6.4) * mm});
            skLineSegment(sketch, "E576", {"start": v(-34.9, -6.4) * mm, "end": v(-34.85, -6.06) * mm});
            skLineSegment(sketch, "E577", {"start": v(-34.85, -6.06) * mm, "end": v(-35.1, -5.69) * mm});
            skLineSegment(sketch, "E578", {"start": v(-35.1, -5.69) * mm, "end": v(-35.37, -5.45) * mm});
            skLineSegment(sketch, "E579", {"start": v(-35.37, -5.45) * mm, "end": v(-35.66, -5.33) * mm});
            skLineSegment(sketch, "E580", {"start": v(-35.66, -5.33) * mm, "end": v(-35.96, -5.32) * mm});
            skLineSegment(sketch, "E581", {"start": v(-35.96, -5.32) * mm, "end": v(-36.26, -5.38) * mm});
            skLineSegment(sketch, "E582", {"start": v(-36.26, -5.38) * mm, "end": v(-36.56, -5.5) * mm});
            skLineSegment(sketch, "E583", {"start": v(-36.56, -5.5) * mm, "end": v(-36.85, -5.68) * mm});
            skLineSegment(sketch, "E584", {"start": v(-36.85, -5.68) * mm, "end": v(-37.13, -5.87) * mm});
            skLineSegment(sketch, "E585", {"start": v(-37.13, -5.87) * mm, "end": v(-37.21, -5.68) * mm});
            skLineSegment(sketch, "E586", {"start": v(-37.21, -5.68) * mm, "end": v(-37.32, -5.53) * mm});
            skLineSegment(sketch, "E587", {"start": v(-37.32, -5.53) * mm, "end": v(-37.44, -5.42) * mm});
            skLineSegment(sketch, "E588", {"start": v(-37.44, -5.42) * mm, "end": v(-37.59, -5.33) * mm});
            skLineSegment(sketch, "E589", {"start": v(-37.59, -5.33) * mm, "end": v(-37.75, -5.27) * mm});
            skLineSegment(sketch, "E590", {"start": v(-37.75, -5.27) * mm, "end": v(-37.92, -5.22) * mm});
            skLineSegment(sketch, "E591", {"start": v(-37.92, -5.22) * mm, "end": v(-38.1, -5.18) * mm});
            skLineSegment(sketch, "E592", {"start": v(-38.1, -5.18) * mm, "end": v(-38.27, -5.15) * mm});
            skLineSegment(sketch, "E593", {"start": v(-38.27, -5.15) * mm, "end": v(-38.44, -5.12) * mm});
            skLineSegment(sketch, "E594", {"start": v(-38.44, -5.12) * mm, "end": v(-38.61, -5.07) * mm});
            skLineSegment(sketch, "E595", {"start": v(-38.61, -5.07) * mm, "end": v(-38.77, -5.01) * mm});
            skLineSegment(sketch, "E596", {"start": v(-38.77, -5.01) * mm, "end": v(-38.92, -4.93) * mm});
            skLineSegment(sketch, "E597", {"start": v(-38.92, -4.93) * mm, "end": v(-39.05, -4.82) * mm});
            skLineSegment(sketch, "E598", {"start": v(-39.05, -4.82) * mm, "end": v(-39.15, -4.68) * mm});
            skLineSegment(sketch, "E599", {"start": v(-39.15, -4.68) * mm, "end": v(-39.23, -4.5) * mm});
            skLineSegment(sketch, "E600", {"start": v(-39.23, -4.5) * mm, "end": v(-39.29, -4.27) * mm});
            skLineSegment(sketch, "E601", {"start": v(-39.29, -4.27) * mm, "end": v(-39.43, -4.47) * mm});
            skLineSegment(sketch, "E602", {"start": v(-39.43, -4.47) * mm, "end": v(-39.6, -4.62) * mm});
            skLineSegment(sketch, "E603", {"start": v(-39.6, -4.62) * mm, "end": v(-39.8, -4.75) * mm});
            skLineSegment(sketch, "E604", {"start": v(-39.8, -4.75) * mm, "end": v(-40.02, -4.86) * mm});
            skLineSegment(sketch, "E605", {"start": v(-40.02, -4.86) * mm, "end": v(-40.24, -4.95) * mm});
            skLineSegment(sketch, "E606", {"start": v(-40.24, -4.95) * mm, "end": v(-40.46, -5.03) * mm});
            skLineSegment(sketch, "E607", {"start": v(-40.46, -5.03) * mm, "end": v(-40.67, -5.1) * mm});
            skLineSegment(sketch, "E608", {"start": v(-40.67, -5.1) * mm, "end": v(-40.88, -5.19) * mm});
            skLineSegment(sketch, "E609", {"start": v(-40.88, -5.19) * mm, "end": v(-41.06, -5.28) * mm});
            skLineSegment(sketch, "E610", {"start": v(-41.06, -5.28) * mm, "end": v(-41.22, -5.38) * mm});
            skLineSegment(sketch, "E611", {"start": v(-41.22, -5.38) * mm, "end": v(-41.34, -5.5) * mm});
            skLineSegment(sketch, "E612", {"start": v(-41.34, -5.5) * mm, "end": v(-41.42, -5.66) * mm});
            skLineSegment(sketch, "E613", {"start": v(-41.42, -5.66) * mm, "end": v(-41.46, -5.85) * mm});
            skLineSegment(sketch, "E614", {"start": v(-41.46, -5.85) * mm, "end": v(-41.44, -6.08) * mm});
            skLineSegment(sketch, "E615", {"start": v(-41.44, -6.08) * mm, "end": v(-41.36, -6.35) * mm});
            skLineSegment(sketch, "E616", {"start": v(-41.36, -6.35) * mm, "end": v(-41.2, -6.67) * mm});
            skLineSegment(sketch, "E617", {"start": v(-41.2, -6.67) * mm, "end": v(-41, -7.46) * mm});
            skLineSegment(sketch, "E618", {"start": v(-41, -7.46) * mm, "end": v(-40.78, -8.25) * mm});
            skLineSegment(sketch, "E619", {"start": v(-40.78, -8.25) * mm, "end": v(-40.53, -9.03) * mm});
            skLineSegment(sketch, "E620", {"start": v(-40.53, -9.03) * mm, "end": v(-40.26, -9.8) * mm});
            skLineSegment(sketch, "E621", {"start": v(-40.26, -9.8) * mm, "end": v(-39.95, -10.56) * mm});
            skLineSegment(sketch, "E622", {"start": v(-39.95, -10.56) * mm, "end": v(-39.6, -11.3) * mm});
            skLineSegment(sketch, "E623", {"start": v(-39.6, -11.3) * mm, "end": v(-39.2, -12.01) * mm});
            skLineSegment(sketch, "E624", {"start": v(-39.2, -12.01) * mm, "end": v(-38.76, -12.7) * mm});
            skLineSegment(sketch, "E625", {"start": v(-38.76, -12.7) * mm, "end": v(-38.72, -12.85) * mm});
            skLineSegment(sketch, "E626", {"start": v(-38.72, -12.85) * mm, "end": v(-38.65, -12.97) * mm});
            skLineSegment(sketch, "E627", {"start": v(-38.65, -12.97) * mm, "end": v(-38.57, -13.06) * mm});
            skLineSegment(sketch, "E628", {"start": v(-38.57, -13.06) * mm, "end": v(-38.47, -13.12) * mm});
            skLineSegment(sketch, "E629", {"start": v(-38.47, -13.12) * mm, "end": v(-38.37, -13.18) * mm});
            skLineSegment(sketch, "E630", {"start": v(-38.37, -13.18) * mm, "end": v(-38.26, -13.21) * mm});
            skLineSegment(sketch, "E631", {"start": v(-38.26, -13.21) * mm, "end": v(-38.14, -13.25) * mm});
            skLineSegment(sketch, "E632", {"start": v(-38.14, -13.25) * mm, "end": v(-38.03, -13.28) * mm});
            skLineSegment(sketch, "E633", {"start": v(-38.03, -13.28) * mm, "end": v(-37.93, -13.3) * mm});
            skLineSegment(sketch, "E634", {"start": v(-37.93, -13.3) * mm, "end": v(-37.84, -13.35) * mm});
            skLineSegment(sketch, "E635", {"start": v(-37.84, -13.35) * mm, "end": v(-37.76, -13.4) * mm});
            skLineSegment(sketch, "E636", {"start": v(-37.76, -13.4) * mm, "end": v(-37.7, -13.47) * mm});
            skLineSegment(sketch, "E637", {"start": v(-37.7, -13.47) * mm, "end": v(-37.65, -13.56) * mm});
            skLineSegment(sketch, "E638", {"start": v(-37.65, -13.56) * mm, "end": v(-37.64, -13.68) * mm});
            skLineSegment(sketch, "E639", {"start": v(-37.64, -13.68) * mm, "end": v(-37.65, -13.84) * mm});
            skLineSegment(sketch, "E640", {"start": v(-37.65, -13.84) * mm, "end": v(-37.7, -14.03) * mm});
            skSolve(sketch);
        }
        {
            var Q0;
            Q0=makeQuery(id+"F8.imprint","IMPRINT",FACE,{"disambiguationData":[TD([[makeQuery(id+"F8.imprint","IMPRINT",EDGE,{"derivedFrom":sQuery(id+"F8.wireOp",EDGE,"E160")}),1.0]])]});
            extrude(context, id + "F9", {"entities" : qUnion([Q0]), "operationType" : NewBodyOperationType.REMOVE, "endBound" : BoundingType.UP_TO_NEXT, "oppositeDirection" : true, "depth" : 25 * mm});
        }
    });
